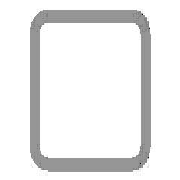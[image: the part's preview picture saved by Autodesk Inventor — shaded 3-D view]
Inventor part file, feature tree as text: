
AUTODESK INVENTOR PART (.ipt)
format: ipt  version: 2024 (Build 280153000, 153)  size: 129,024 bytes
history: native  units: mm (DEFAULTED — no unit token found)
features: other x4, extrude x1, sketch x1, plane x1
ambient origin geometry x8: Origin, YZ Plane, XZ Plane, XY Plane, X Axis, Y Axis, Z Axis, Center Point
bodies: Solid1 (feature_tree)
feature tree (7):
  parser-record x1  (decoder bookkeeping rows leaked as tree rows — omitted from the tree; the rows remain in map.json)
  other  "Driven Length"
  other  "Plano inicial"
  other  "Plano final"
  extrude  "Cuerpo"  TaperAngle=0.0deg  [1 undecoded]
  sketch  "Sketch3"  dims[d3=1890.0mm d4=0.0mm d10=50.8mm d11=50.8mm d12=3.175mm d13=-0.0mm d14=1890.0mm d15=25.4mm d16=25.4mm d17=6.35mm d18=90.0deg d19=1890.0mm]
  plane  "Work Plane3"
note: 1 required parameter value undecoded (feature->parameter linkage not recoverable at this tier; creation-order binding heuristic only, values carry confidence <= 0.55)
